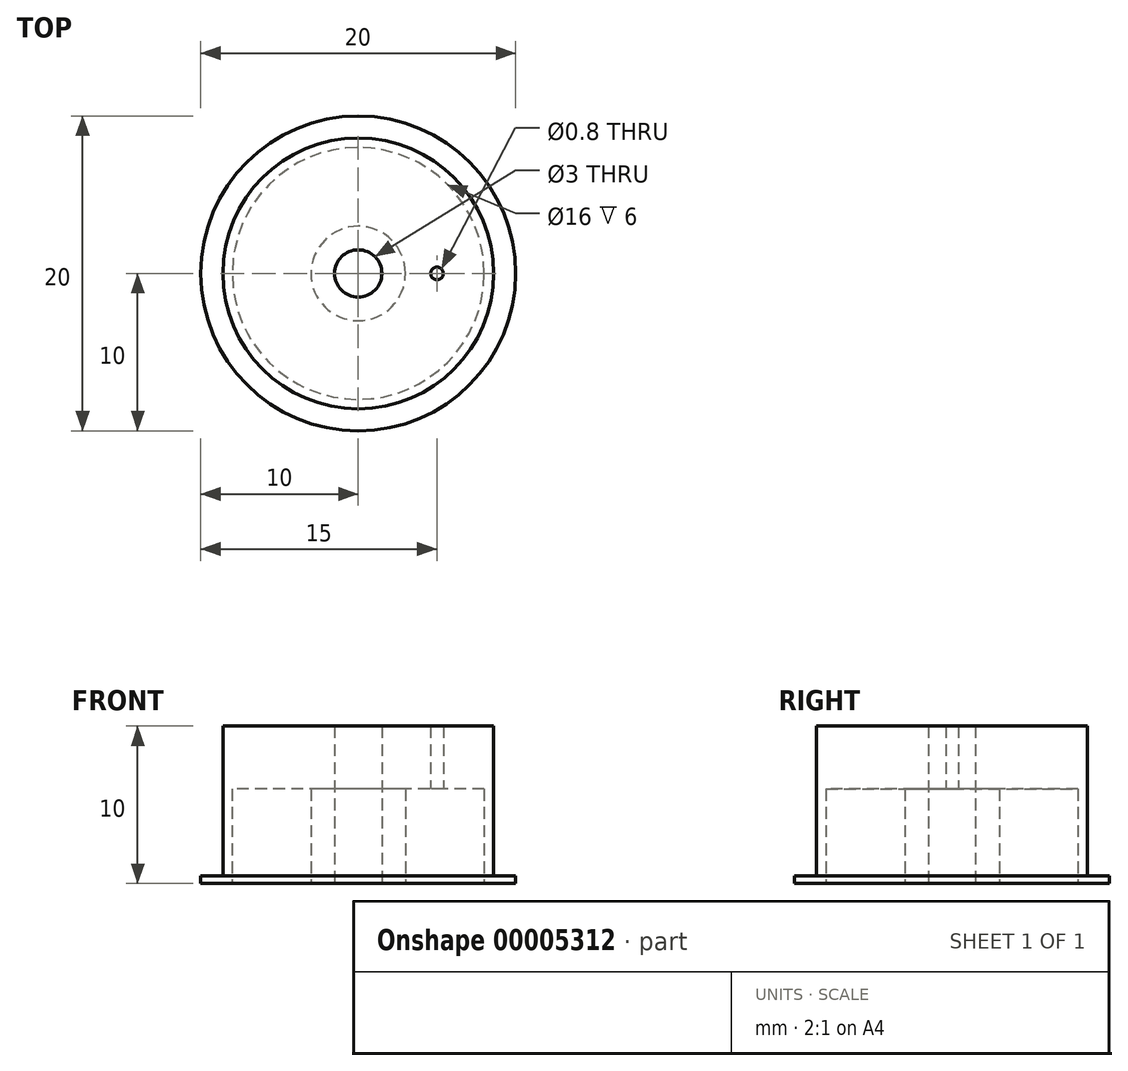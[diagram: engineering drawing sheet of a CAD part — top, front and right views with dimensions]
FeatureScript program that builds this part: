
annotation { "Feature Type Name" : "Feature", "Feature Type Description" : "" }
export const myFeature = defineFeature(function(context is Context, id is Id, definition is map)
    precondition{}
    {
        {
            var Q0;
            Q0=qCreatedBy(makeId("Top.planeOp"),FACE);
            var sketch = newSketch(context, id + "F0", { "sketchPlane" : qUnion([Q0])});
            skCircle(sketch, "E0", {"center": v(0, 0) * mm, "radius": 1.5 * mm});
            skCircle(sketch, "E1", {"center": v(0, 0) * mm, "radius": 3 * mm});
            skCircle(sketch, "E2", {"center": v(0, 0) * mm, "radius": 10 * mm});
            skCircle(sketch, "E3", {"center": v(0, 0) * mm, "radius": 8 * mm});
            skCircle(sketch, "E4", {"center": v(0, 0) * mm, "radius": 8.6 * mm});
            skCircle(sketch, "E5", {"center": v(5, 0) * mm, "radius": 0.4 * mm});
            skSolve(sketch);
        }
        {
            var Q0;
            Q0=makeQuery(id+"F0.imprint","IMPRINT",FACE,{"disambiguationData":[TD([[makeQuery(id+"F0.imprint","IMPRINT",EDGE,{"derivedFrom":sQuery(id+"F0.wireOp",EDGE,"E3")}),-1.0]])]});
            var Q1;
            Q1=makeQuery(id+"F0.imprint","IMPRINT",FACE,{"disambiguationData":[TD([[makeQuery(id+"F0.imprint","IMPRINT",EDGE,{"derivedFrom":sQuery(id+"F0.wireOp",EDGE,"E1")}),-1.0]])]});
            var Q2;
            Q2=makeQuery(id+"F0.imprint","IMPRINT",FACE,{"disambiguationData":[TD([[makeQuery(id+"F0.imprint","IMPRINT",EDGE,{"derivedFrom":sQuery(id+"F0.wireOp",EDGE,"E0")}),-1.0]])]});
            extrude(context, id + "F1", {"entities" : qUnion([Q0, Q1, Q2]), "depth" : 10 * mm});
        }
        {
            var Q0;
            Q0=makeQuery(id+"F0.imprint","IMPRINT",FACE,{"disambiguationData":[TD([[makeQuery(id+"F0.imprint","IMPRINT",EDGE,{"derivedFrom":sQuery(id+"F0.wireOp",EDGE,"E2")}),1.0]])]});
            extrude(context, id + "F2", {"entities" : qUnion([Q0]), "operationType" : NewBodyOperationType.ADD, "depth" : 0.5 * mm});
        }
        {
            var Q0;
            Q0=makeQuery(id+"F0.imprint","IMPRINT",FACE,{"disambiguationData":[TD([[makeQuery(id+"F0.imprint","IMPRINT",EDGE,{"derivedFrom":sQuery(id+"F0.wireOp",EDGE,"E1")}),-1.0]])]});
            extrude(context, id + "F3", {"entities" : qUnion([Q0]), "operationType" : NewBodyOperationType.REMOVE, "depth" : 6 * mm});
        }
    });
